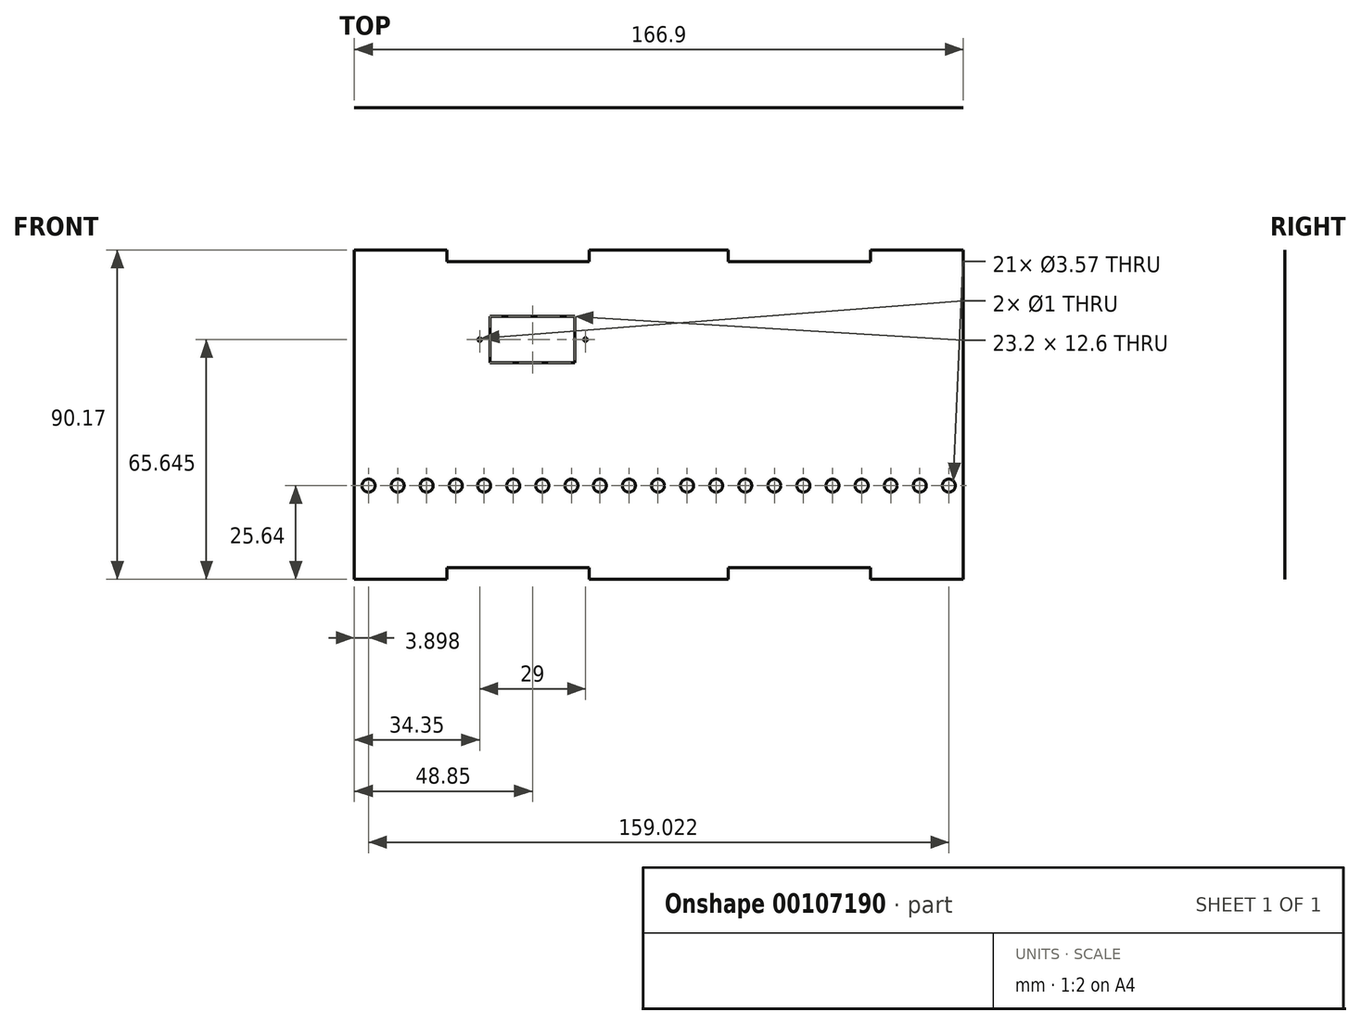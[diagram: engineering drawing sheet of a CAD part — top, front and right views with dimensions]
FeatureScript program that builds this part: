
annotation { "Feature Type Name" : "Feature", "Feature Type Description" : "" }
export const myFeature = defineFeature(function(context is Context, id is Id, definition is map)
    precondition{}
    {
        {
            var Q0;
            Q0=qCreatedBy(makeId("Front.planeOp"),FACE);
            var sketch = newSketch(context, id + "F0", { "sketchPlane" : qUnion([Q0])});
            skPoint(sketch, "E0.middle", {"position": v(0, 0) * mm});
            skCircle(sketch, "E1", {"center": v(0, 0) * mm, "radius": 1.79 * mm});
            skCircle(sketch, "E2.1.0.0", {"center": v(7.97, 0) * mm, "radius": 1.79 * mm});
            skCircle(sketch, "E2.2.0.0", {"center": v(15.94, 0) * mm, "radius": 1.79 * mm});
            skCircle(sketch, "E2.3.0.0", {"center": v(23.91, 0) * mm, "radius": 1.79 * mm});
            skCircle(sketch, "E2.4.0.0", {"center": v(31.88, 0) * mm, "radius": 1.79 * mm});
            skCircle(sketch, "E2.5.0.0", {"center": v(39.85, 0) * mm, "radius": 1.79 * mm});
            skCircle(sketch, "E2.6.0.0", {"center": v(47.82, 0) * mm, "radius": 1.79 * mm});
            skCircle(sketch, "E2.7.0.0", {"center": v(55.8, 0) * mm, "radius": 1.79 * mm});
            skCircle(sketch, "E2.8.0.0", {"center": v(63.76, 0) * mm, "radius": 1.79 * mm});
            skCircle(sketch, "E2.9.0.0", {"center": v(71.73, 0) * mm, "radius": 1.79 * mm});
            skLineSegment(sketch, "E2.direction1", {"start": v(0, 0) * mm, "end": v(7.97, 0) * mm, "construction": true});
            skCircle(sketch, "E3.MirrorC", {"center": v(-7.8, 0) * mm, "radius": 1.79 * mm});
            skCircle(sketch, "E4.MirrorC", {"center": v(-15.76, 0) * mm, "radius": 1.79 * mm});
            skCircle(sketch, "E5.MirrorC", {"center": v(-23.73, 0) * mm, "radius": 1.79 * mm});
            skCircle(sketch, "E6.MirrorC", {"center": v(-31.7, 0) * mm, "radius": 1.79 * mm});
            skCircle(sketch, "E7.MirrorC", {"center": v(-63.38, 0) * mm, "radius": 1.79 * mm});
            skCircle(sketch, "E8.MirrorC", {"center": v(-47.44, 0) * mm, "radius": 1.79 * mm});
            skCircle(sketch, "E9.MirrorC", {"center": v(-55.41, 0) * mm, "radius": 1.79 * mm});
            skCircle(sketch, "E10.MirrorC", {"center": v(-39.47, 0) * mm, "radius": 1.79 * mm});
            skLineSegment(sketch, "E11", {"start": v(-67.28, -22.47) * mm, "end": v(-67.28, 61.13) * mm});
            skPoint(sketch, "E11.startSnap0", {"position": v(-67.28, 9.21) * mm});
            skPoint(sketch, "E11.endSnap0", {"position": v(-67.28, 33.41) * mm});
            skLineSegment(sketch, "E12", {"start": v(-67.28, 61.35) * mm, "end": v(-67.28, 61.13) * mm});
            skLineSegment(sketch, "E13.bottom", {"start": v(99.63, 61.35) * mm, "end": v(74.23, 61.35) * mm});
            skLineSegment(sketch, "E13.top", {"start": v(99.63, 64.53) * mm, "end": v(74.23, 64.53) * mm});
            skLineSegment(sketch, "E13.left", {"start": v(99.63, 61.35) * mm, "end": v(99.63, 64.53) * mm});
            skLineSegment(sketch, "E13.right", {"start": v(74.23, 61.35) * mm, "end": v(74.23, 64.53) * mm});
            skLineSegment(sketch, "E14.bottom", {"start": v(35.22, 61.35) * mm, "end": v(-2.88, 61.35) * mm});
            skLineSegment(sketch, "E14.top", {"start": v(35.22, 64.53) * mm, "end": v(-2.88, 64.53) * mm});
            skLineSegment(sketch, "E14.left", {"start": v(35.22, 61.35) * mm, "end": v(35.22, 64.53) * mm});
            skLineSegment(sketch, "E14.right", {"start": v(-2.88, 61.35) * mm, "end": v(-2.88, 64.53) * mm});
            skLineSegment(sketch, "E15.bottom", {"start": v(-67.28, 61.35) * mm, "end": v(-41.88, 61.35) * mm});
            skLineSegment(sketch, "E15.top", {"start": v(-67.28, 64.53) * mm, "end": v(-41.88, 64.53) * mm});
            skLineSegment(sketch, "E15.left", {"start": v(-67.28, 61.35) * mm, "end": v(-67.28, 64.53) * mm});
            skLineSegment(sketch, "E15.right", {"start": v(-41.88, 61.35) * mm, "end": v(-41.88, 64.53) * mm});
            skPoint(sketch, "E16", {"position": v(16.17, 61.35) * mm});
            skLineSegment(sketch, "E17.bottom", {"start": v(-67.28, -22.47) * mm, "end": v(-41.88, -22.47) * mm});
            skLineSegment(sketch, "E17.top", {"start": v(-67.28, -25.64) * mm, "end": v(-41.88, -25.64) * mm});
            skLineSegment(sketch, "E17.left", {"start": v(-67.28, -22.47) * mm, "end": v(-67.28, -25.64) * mm});
            skLineSegment(sketch, "E17.right", {"start": v(-41.88, -22.47) * mm, "end": v(-41.88, -25.64) * mm});
            skLineSegment(sketch, "E18.bottom", {"start": v(-2.88, -22.47) * mm, "end": v(35.22, -22.47) * mm});
            skLineSegment(sketch, "E18.top", {"start": v(-2.88, -25.64) * mm, "end": v(35.22, -25.64) * mm});
            skLineSegment(sketch, "E18.left", {"start": v(-2.88, -22.47) * mm, "end": v(-2.88, -25.64) * mm});
            skLineSegment(sketch, "E18.right", {"start": v(35.22, -22.47) * mm, "end": v(35.22, -25.64) * mm});
            skLineSegment(sketch, "E19.bottom", {"start": v(99.63, -22.47) * mm, "end": v(74.23, -22.47) * mm});
            skLineSegment(sketch, "E19.top", {"start": v(99.63, -25.64) * mm, "end": v(74.23, -25.64) * mm});
            skLineSegment(sketch, "E19.left", {"start": v(99.63, -22.47) * mm, "end": v(99.63, -25.64) * mm});
            skLineSegment(sketch, "E19.right", {"start": v(74.23, -22.47) * mm, "end": v(74.23, -25.64) * mm});
            skPoint(sketch, "E20", {"position": v(16.17, -22.47) * mm});
            skCircle(sketch, "E21.7.0.0", {"center": v(79.7, 0) * mm, "radius": 1.79 * mm});
            skCircle(sketch, "E22.7.0.0", {"center": v(87.67, 0) * mm, "radius": 1.79 * mm});
            skCircle(sketch, "E23.7.0.0", {"center": v(95.64, 0) * mm, "radius": 1.79 * mm});
            skLineSegment(sketch, "E24", {"start": v(99.62, -22.47) * mm, "end": v(99.62, 61.35) * mm});
            skPoint(sketch, "E24.startSnap0", {"position": v(99.62, 3.81) * mm});
            skLineSegment(sketch, "E25", {"start": v(-67.28, 61.35) * mm, "end": v(99.63, 61.35) * mm});
            skLineSegment(sketch, "E26", {"start": v(99.63, -22.47) * mm, "end": v(-67.28, -22.47) * mm});
            skLineSegment(sketch, "E27.bottom", {"start": v(-30.03, 46.3) * mm, "end": v(-6.83, 46.3) * mm});
            skLineSegment(sketch, "E27.top", {"start": v(-30.03, 33.7) * mm, "end": v(-6.83, 33.7) * mm});
            skLineSegment(sketch, "E27.left", {"start": v(-30.03, 46.3) * mm, "end": v(-30.03, 33.7) * mm});
            skLineSegment(sketch, "E27.right", {"start": v(-6.83, 46.3) * mm, "end": v(-6.83, 33.7) * mm});
            skPoint(sketch, "E28", {"position": v(-23.73, 46.3) * mm});
            skLineSegment(sketch, "E29", {"start": v(-18.43, 46.3) * mm, "end": v(-18.43, 33.7) * mm});
            skPoint(sketch, "E30.startSnap0", {"position": v(-18.43, 40) * mm});
            skCircle(sketch, "E31", {"center": v(-3.93, 40) * mm, "radius": 0.5 * mm});
            skCircle(sketch, "E32", {"center": v(-32.93, 40) * mm, "radius": 0.5 * mm});
            skSolve(sketch);
        }
        {
            var Q0;
            Q0=makeQuery(id+"F0.imprint","IMPRINT",FACE,{"disambiguationData":[TD([[makeQuery(id+"F0.imprint","IMPRINT",EDGE,{"derivedFrom":sQuery(id+"F0.wireOp",EDGE,"E15.top")}),-1.0]])]});
            var Q1;
            Q1=makeQuery(id+"F0.imprint","IMPRINT",FACE,{"disambiguationData":[TD([[makeQuery(id+"F0.imprint","IMPRINT",EDGE,{"derivedFrom":sQuery(id+"F0.wireOp",EDGE,"E14.top")}),1.0]])]});
            var Q2;
            Q2=makeQuery(id+"F0.imprint","IMPRINT",FACE,{"disambiguationData":[TD([[makeQuery(id+"F0.imprint","IMPRINT",EDGE,{"derivedFrom":sQuery(id+"F0.wireOp",EDGE,"E13.top")}),1.0]])]});
            var Q3;
            Q3=makeQuery(id+"F0.imprint","IMPRINT",FACE,{"disambiguationData":[TD([[makeQuery(id+"F0.imprint","IMPRINT",EDGE,{"derivedFrom":sQuery(id+"F0.wireOp",EDGE,"E19.top")}),-1.0]])]});
            var Q4;
            Q4=makeQuery(id+"F0.imprint","IMPRINT",FACE,{"disambiguationData":[TD([[makeQuery(id+"F0.imprint","IMPRINT",EDGE,{"derivedFrom":sQuery(id+"F0.wireOp",EDGE,"E18.top")}),1.0]])]});
            var Q5;
            Q5=makeQuery(id+"F0.imprint","IMPRINT",FACE,{"disambiguationData":[TD([[makeQuery(id+"F0.imprint","IMPRINT",EDGE,{"derivedFrom":sQuery(id+"F0.wireOp",EDGE,"E17.top")}),1.0]])]});
            var Q6;
            Q6=makeQuery(id+"F0.imprint","IMPRINT",FACE,{"disambiguationData":[TD([[makeQuery(id+"F0.imprint","IMPRINT",EDGE,{"derivedFrom":sQuery(id+"F0.wireOp",EDGE,"E1")}),-1.0]])]});
            extrude(context, id + "F1", {"entities" : qUnion([Q0, Q1, Q2, Q3, Q4, Q5, Q6]), "depth" : 1 / 203.2 * mm});
        }
    });
